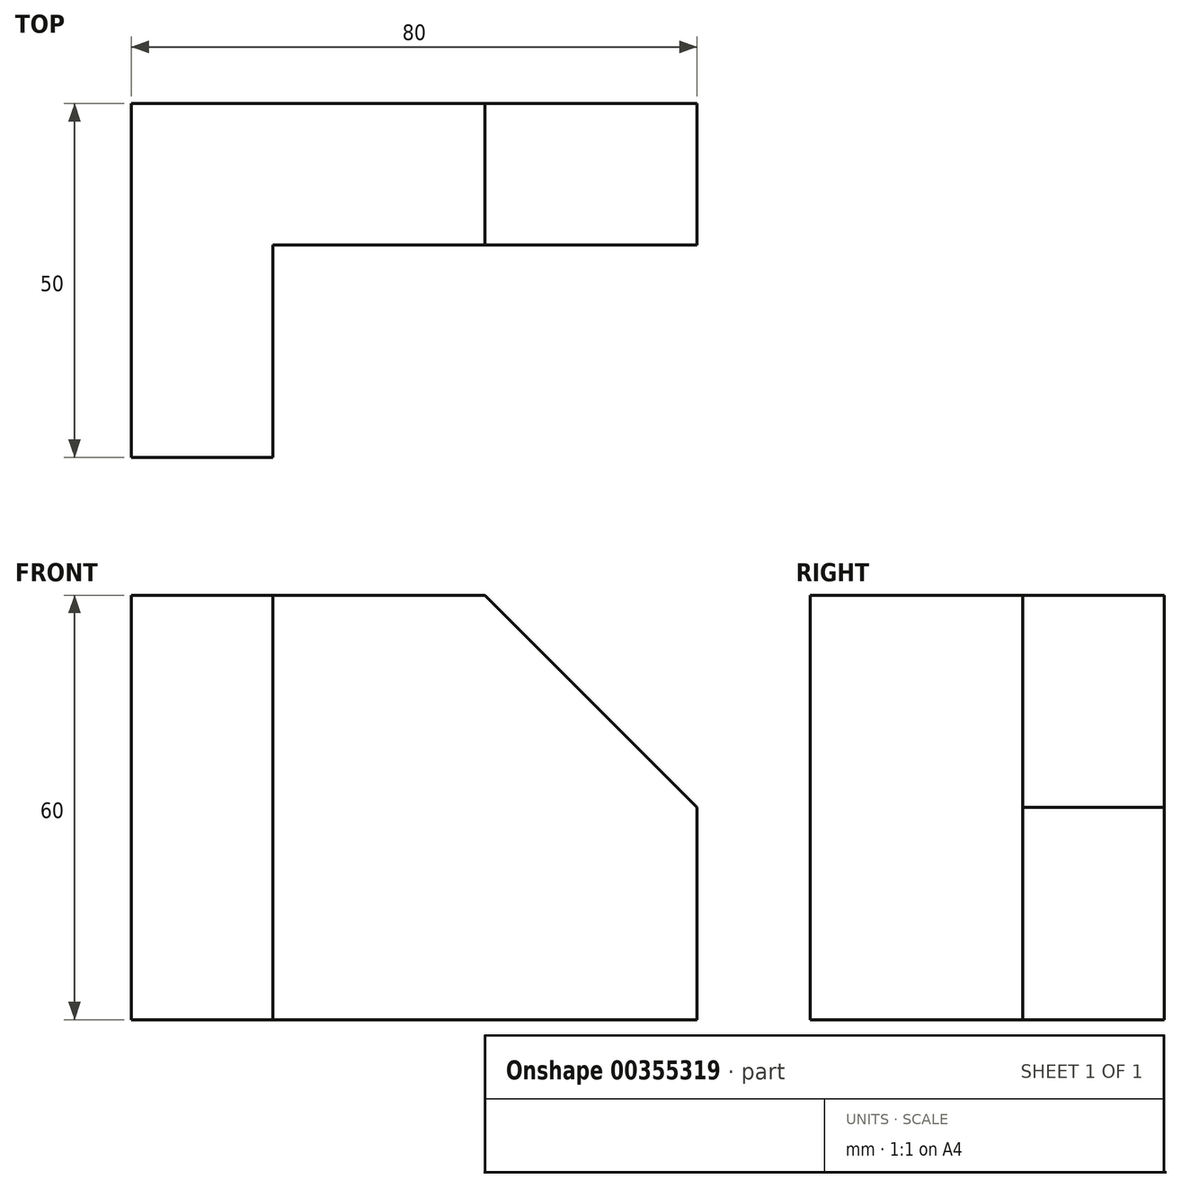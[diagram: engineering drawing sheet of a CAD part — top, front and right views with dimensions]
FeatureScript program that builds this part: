
annotation { "Feature Type Name" : "Feature", "Feature Type Description" : "" }
export const myFeature = defineFeature(function(context is Context, id is Id, definition is map)
    precondition{}
    {
        {
            var Q0;
            Q0=qCreatedBy(makeId("Front.planeOp"),FACE);
            var sketch = newSketch(context, id + "F0", { "sketchPlane" : qUnion([Q0])});
            skLineSegment(sketch, "E0.bottom", {"start": v(-40, 30) * mm, "end": v(40, 30) * mm});
            skLineSegment(sketch, "E0.top", {"start": v(-40, -30) * mm, "end": v(40, -30) * mm});
            skLineSegment(sketch, "E0.left", {"start": v(-40, 30) * mm, "end": v(-40, -30) * mm});
            skLineSegment(sketch, "E0.right", {"start": v(40, 30) * mm, "end": v(40, -30) * mm});
            skPoint(sketch, "E0.middle", {"position": v(0, 0) * mm});
            skSolve(sketch);
        }
        {
            var Q0;
            Q0 = qSketchRegion(id + "F0", true);
            extrude(context, id + "F1", {"entities" : qUnion([Q0]), "depth" : 20 * mm});
        }
        {
            var Q0;
            Q0=makeQuery(id+"F1.opExtrude","CAP_FACE",FACE,{"disambiguationData":[OSD([sQuery(id+"F0.wireOp",EDGE,"E0.bottom"),sQuery(id+"F0.wireOp",EDGE,"E0.top"),sQuery(id+"F0.wireOp",EDGE,"E0.left"),sQuery(id+"F0.wireOp",EDGE,"E0.right")])],"isStart":false});
            var sketch = newSketch(context, id + "F2", { "sketchPlane" : qUnion([Q0])});
            skLineSegment(sketch, "E1", {"start": v(-20, 30) * mm, "end": v(-20, -30) * mm});
            skSolve(sketch);
        }
        {
            var Q0;
            {var subQ0=sQuery(id+"F2.wireOp",EDGE,"E1");Q0=makeQuery(id+"F2.imprint","IMPRINT",FACE,{"disambiguationData":[TD([[makeQuery(id+"F2.imprint","IMPRINT",EDGE,{"derivedFrom":subQ0}),-1.0]])]});}
            extrude(context, id + "F3", {"entities" : qUnion([Q0]), "operationType" : NewBodyOperationType.ADD, "depth" : 30 * mm});
        }
        {
            var Q0;
            Q0=makeQuery(id+"F1.opExtrude","CAP_FACE",FACE,{"disambiguationData":[OSD([sQuery(id+"F0.wireOp",EDGE,"E0.bottom"),sQuery(id+"F0.wireOp",EDGE,"E0.top"),sQuery(id+"F0.wireOp",EDGE,"E0.left"),sQuery(id+"F0.wireOp",EDGE,"E0.right")])],"isStart":false});
            var sketch = newSketch(context, id + "F4", { "sketchPlane" : qUnion([Q0])});
            skLineSegment(sketch, "E2", {"start": v(10, 30) * mm, "end": v(10, -30) * mm, "construction": true});
            skLineSegment(sketch, "E3", {"start": v(40, 0) * mm, "end": v(-4.9, 0) * mm, "construction": true});
            skLineSegment(sketch, "E4", {"start": v(10, 30) * mm, "end": v(40, 0) * mm});
            skSolve(sketch);
        }
        {
            var Q0;
            {var subQ0=sQuery(id+"F4.wireOp",EDGE,"E4");Q0=makeQuery(id+"F4.imprint","IMPRINT",FACE,{"disambiguationData":[TD([[makeQuery(id+"F4.imprint","IMPRINT",EDGE,{"derivedFrom":subQ0}),1.0]])]});}
            extrude(context, id + "F5", {"entities" : qUnion([Q0]), "operationType" : NewBodyOperationType.REMOVE, "endBound" : BoundingType.THROUGH_ALL, "oppositeDirection" : true, "depth" : 20 * mm});
        }
    });
